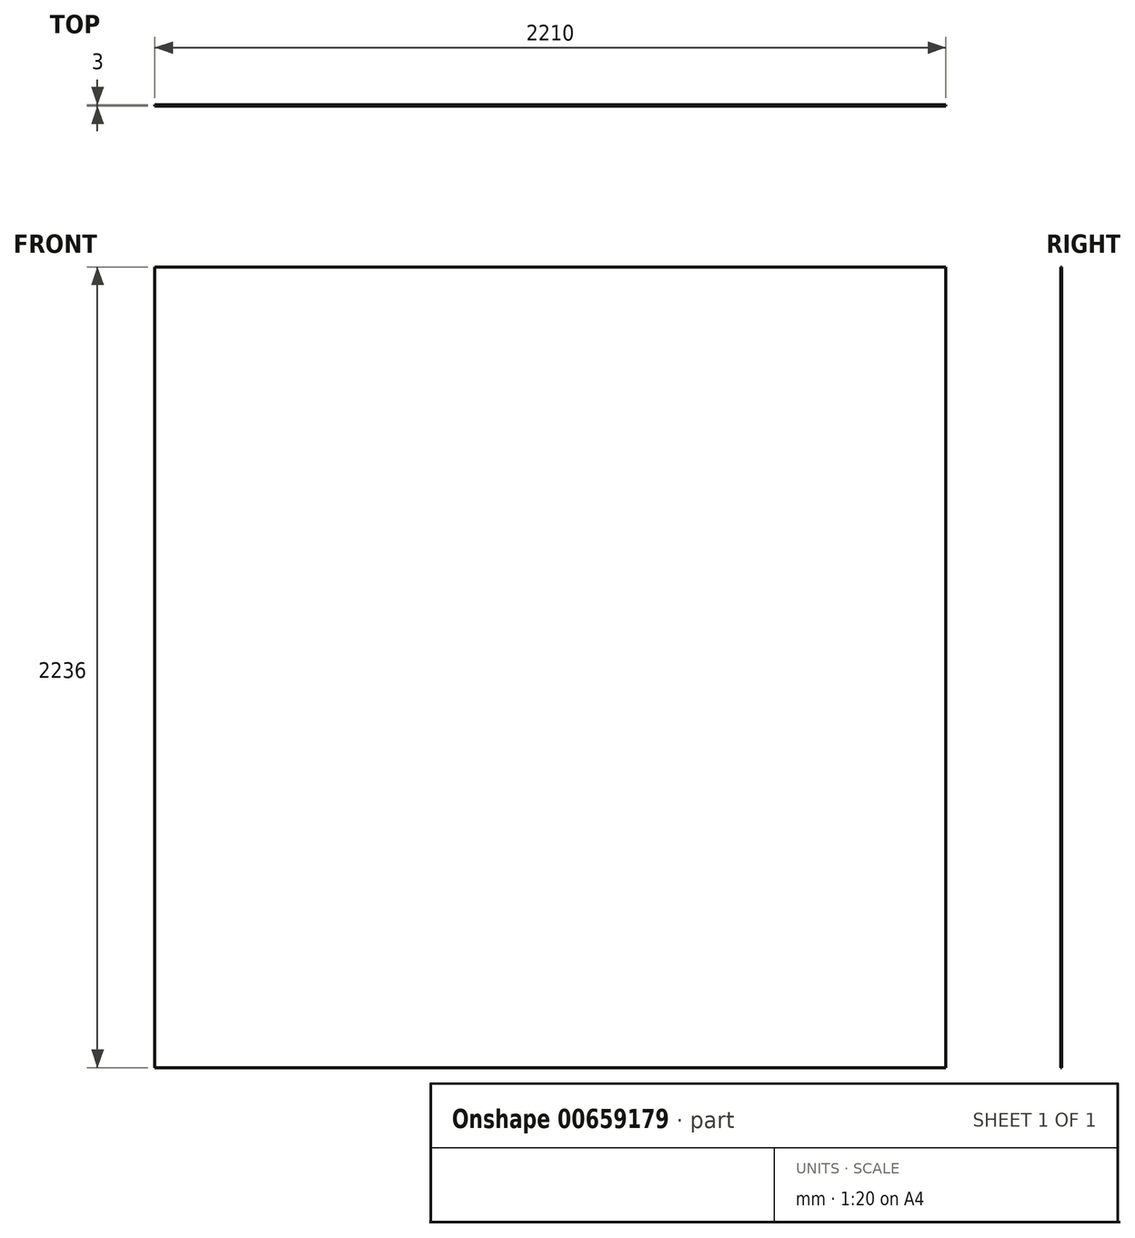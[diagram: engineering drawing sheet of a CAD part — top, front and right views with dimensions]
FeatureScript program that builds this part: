
annotation { "Feature Type Name" : "Feature", "Feature Type Description" : "" }
export const myFeature = defineFeature(function(context is Context, id is Id, definition is map)
    precondition{}
    {
        {
            var Q0;
            Q0=qCreatedBy(makeId("Front.planeOp"),FACE);
            var sketch = newSketch(context, id + "F0", { "sketchPlane" : qUnion([Q0])});
            skLineSegment(sketch, "E0.bottom", {"start": v(-1102.57, 1473.35) * mm, "end": v(1107.43, 1473.35) * mm});
            skLineSegment(sketch, "E0.top", {"start": v(-1102.57, -762.65) * mm, "end": v(1107.43, -762.65) * mm});
            skLineSegment(sketch, "E0.left", {"start": v(-1102.57, 1473.35) * mm, "end": v(-1102.57, -762.65) * mm});
            skLineSegment(sketch, "E0.right", {"start": v(1107.43, 1473.35) * mm, "end": v(1107.43, -762.65) * mm});
            skSolve(sketch);
        }
        {
            var Q0;
            Q0 = qSketchRegion(id + "F0", true);
            extrude(context, id + "F1", {"entities" : qUnion([Q0]), "endBound" : BoundingType.SYMMETRIC, "depth" : 3 * mm, "offsetDistance" : 25 * mm});
        }
    });
